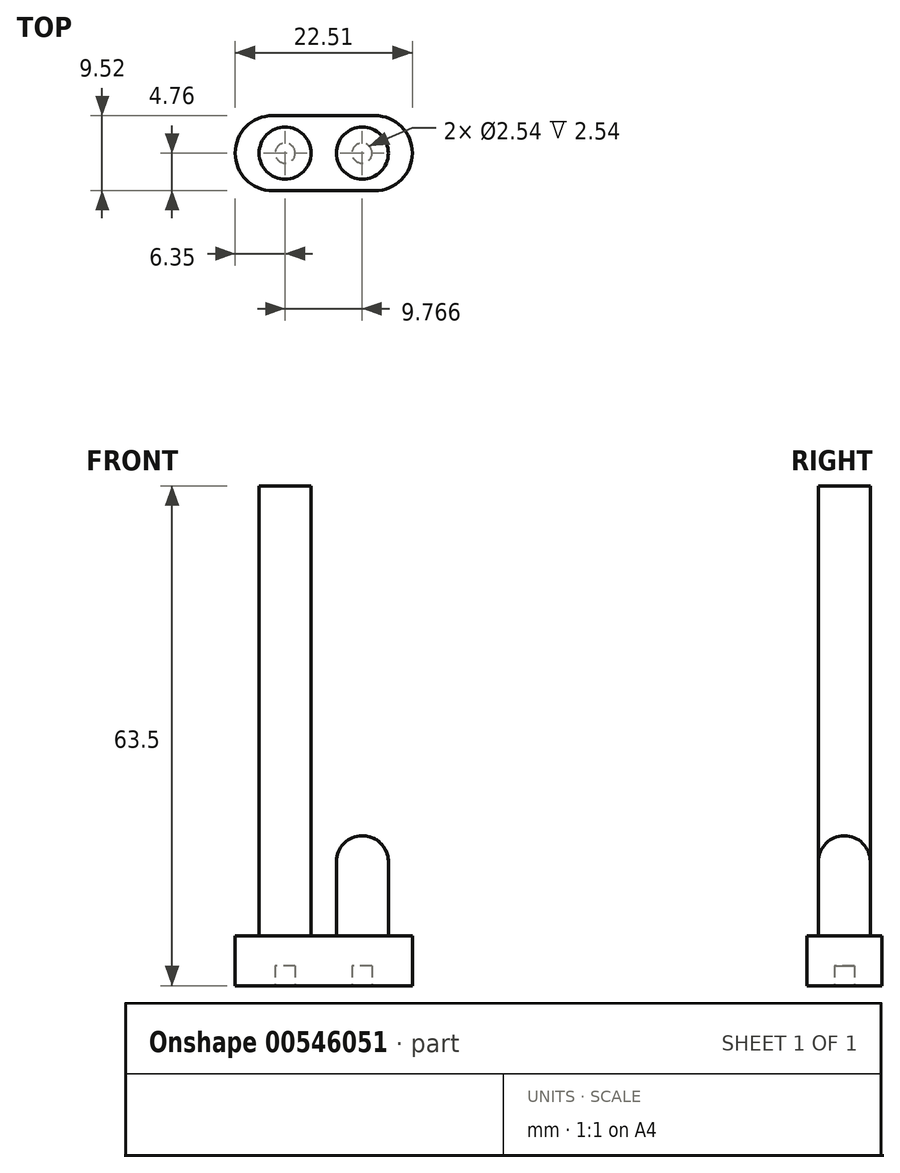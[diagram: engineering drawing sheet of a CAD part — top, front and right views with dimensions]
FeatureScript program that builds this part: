
annotation { "Feature Type Name" : "Feature", "Feature Type Description" : "" }
export const myFeature = defineFeature(function(context is Context, id is Id, definition is map)
    precondition{}
    {
        {
            var Q0;
            Q0=qCreatedBy(makeId("Top.planeOp"),FACE);
            var sketch = newSketch(context, id + "F0", { "sketchPlane" : qUnion([Q0])});
            skCircle(sketch, "E0", {"center": v(0, 0) * mm, "radius": 3.3 * mm});
            skCircle(sketch, "E1", {"center": v(9.8, 0) * mm, "radius": 3.3 * mm});
            skLineSegment(sketch, "E2", {"start": v(3.3, 0) * mm, "end": v(3.17, 0) * mm});
            skLineSegment(sketch, "E3", {"start": v(12.98, 0) * mm, "end": v(13.1, 0) * mm});
            skArc(sketch, "E4", {"start": v(-1.59, 4.76) * mm, "mid": v(-6.35, 0) * mm, "end": v(-1.59, -4.76) * mm});
            skArc(sketch, "E5", {"start": v(11.4, -4.76) * mm, "mid": v(16.16, 0) * mm, "end": v(11.4, 4.76) * mm});
            skLineSegment(sketch, "E6", {"start": v(-1.59, 4.76) * mm, "end": v(11.4, 4.76) * mm});
            skLineSegment(sketch, "E7", {"start": v(11.4, -4.76) * mm, "end": v(-1.59, -4.76) * mm});
            skPoint(sketch, "E8.orphan", {"position": v(-6.35, 0) * mm});
            skPoint(sketch, "E9.orphan", {"position": v(-3.18, 0) * mm});
            skLineSegment(sketch, "E10.trimOffspring", {"start": v(-3.18, 0) * mm, "end": v(-3.3, 0) * mm});
            skPoint(sketch, "E11.start.orphan", {"position": v(12.98, 0) * mm});
            skPoint(sketch, "E12.orphan", {"position": v(16.16, 0) * mm});
            skSolve(sketch);
        }
        {
            var Q0;
            {var subQ0=sQuery(id+"F0.wireOp",EDGE,"E0");var subQ1=makeQuery(id+"F0.imprint","IMPRINT",VERTEX,{"disambiguationData":[OD(0.0)],"derivedFrom":subQ0});Q0=makeQuery(id+"F0.imprint","IMPRINT",FACE,{"disambiguationData":[TD([[makeQuery(id+"F0.imprint","IMPRINT",EDGE,{"disambiguationData":[TD([[subQ1,-1.0]])],"derivedFrom":subQ0}),1.0]])]});}
            extrude(context, id + "F1", {"entities" : qUnion([Q0]), "depth" : 63.5 * mm, "offsetDistance" : 25.4 * mm});
        }
        {
            var Q0;
            Q0=makeQuery(id+"F0.imprint","IMPRINT",FACE,{"disambiguationData":[TD([[makeQuery(id+"F0.imprint","IMPRINT",EDGE,{"derivedFrom":sQuery(id+"F0.wireOp",EDGE,"E1")}),1.0]])]});
            extrude(context, id + "F2", {"entities" : qUnion([Q0]), "depth" : 19.05 * mm, "offsetDistance" : 25.4 * mm});
        }
        {
            var Q0;
            Q0=makeQuery(id+"F0.imprint","IMPRINT",FACE,{"disambiguationData":[TD([[makeQuery(id+"F0.imprint","IMPRINT",EDGE,{"derivedFrom":sQuery(id+"F0.wireOp",EDGE,"E1")}),-1.0]])]});
            extrude(context, id + "F3", {"entities" : qUnion([Q0]), "depth" : 5.08 * mm, "offsetDistance" : 25.4 * mm});
        }
        {
            var Q0;
            Q0=makeQuery(id+"F3.opExtrude","CAP_FACE",FACE,{"disambiguationData":[OSD([sQuery(id+"F0.wireOp",EDGE,"E0"),sQuery(id+"F0.wireOp",EDGE,"E1"),sQuery(id+"F0.wireOp",EDGE,"E4"),sQuery(id+"F0.wireOp",EDGE,"E5"),sQuery(id+"F0.wireOp",EDGE,"E6"),sQuery(id+"F0.wireOp",EDGE,"E7")])],"isStart":false});
            extrude(context, id + "F4", {"entities" : qUnion([Q0]), "operationType" : NewBodyOperationType.ADD, "depth" : 1.27 * mm, "offsetDistance" : 25.4 * mm});
        }
        {
            var Q0;
            Q0=makeQuery(id+"F2.opExtrude","CAP_EDGE",EDGE,{"disambiguationData":[OSD([sQuery(id+"F0.wireOp",EDGE,"E1")])],"isStart":false});
            fillet(context, id + "F5", {"entities" : qUnion([Q0]), "radius" : 3.3 * mm, "tangentPropagation" : true, "allowEdgeOverflow" : false});
        }
        {
            var Q0;
            {var subQ0=sQuery(id+"F0.wireOp",EDGE,"E0");var subQ1=makeQuery(id+"F0.imprint","IMPRINT",VERTEX,{"disambiguationData":[OD(0.0)],"derivedFrom":subQ0});Q0=makeQuery(id+"F0.imprint","IMPRINT",FACE,{"disambiguationData":[TD([[makeQuery(id+"F0.imprint","IMPRINT",EDGE,{"disambiguationData":[TD([[subQ1,-1.0]])],"derivedFrom":subQ0}),1.0]])]});}
            var sketch = newSketch(context, id + "F6", { "sketchPlane" : qUnion([Q0])});
            skCircle(sketch, "E13", {"center": v(0, 0) * mm, "radius": 1.27 * mm});
            skCircle(sketch, "E14", {"center": v(9.77, 0) * mm, "radius": 1.27 * mm});
            skSolve(sketch);
        }
        {
            var Q0;
            Q0 = qSketchRegion(id + "F6", true);
            extrude(context, id + "F7", {"entities" : qUnion([Q0]), "operationType" : NewBodyOperationType.REMOVE, "depth" : 2.54 * mm, "offsetDistance" : 25.4 * mm});
        }
    });
